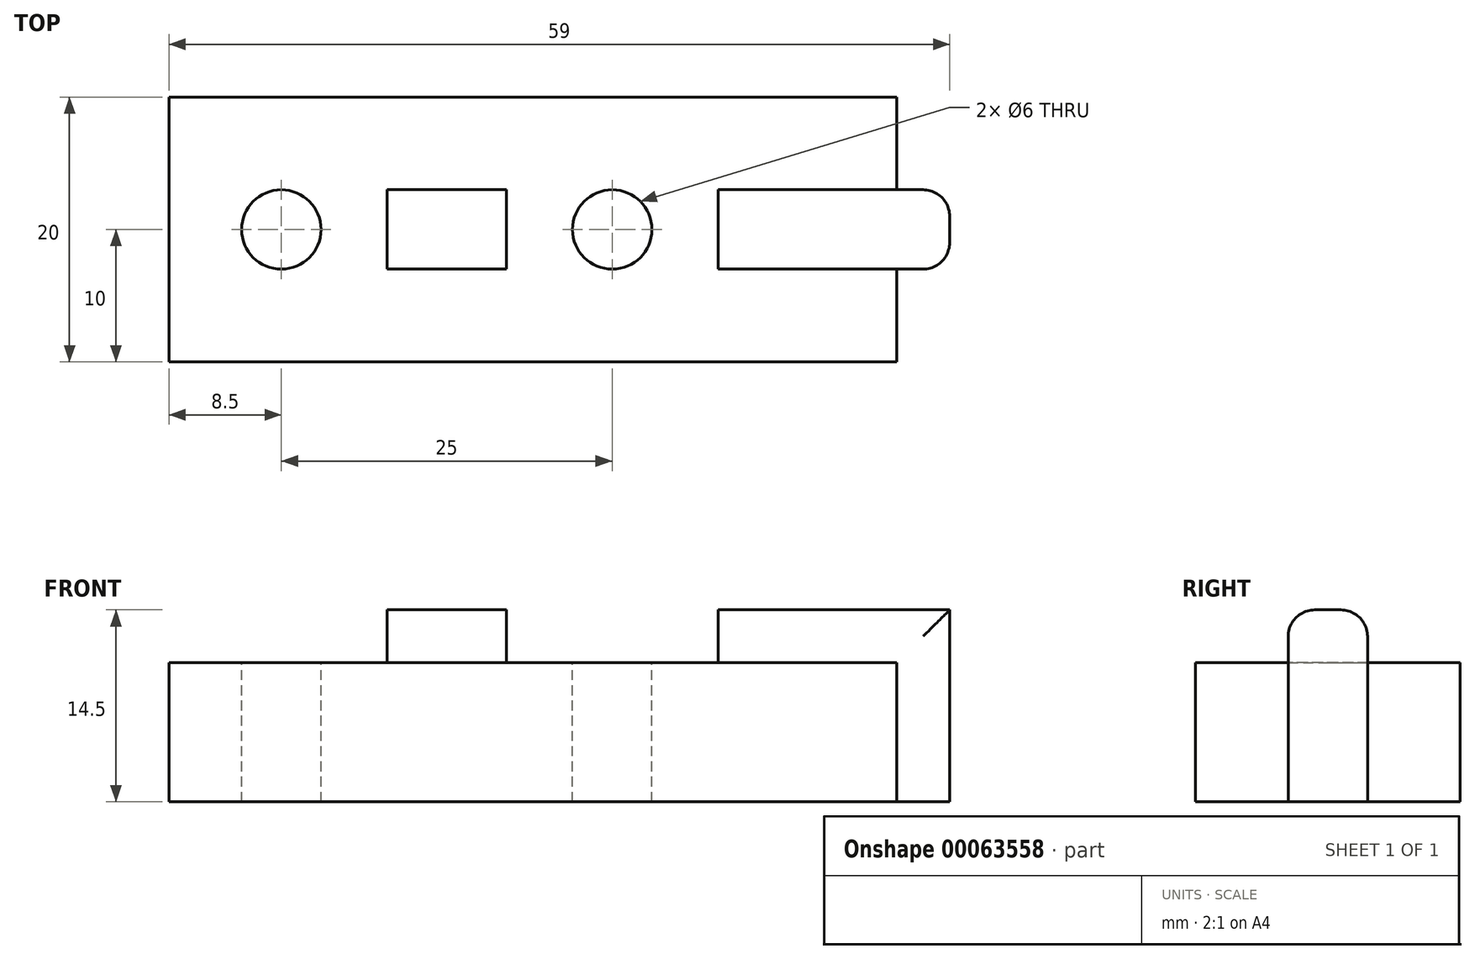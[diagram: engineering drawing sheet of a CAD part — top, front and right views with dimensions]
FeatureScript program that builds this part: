
annotation { "Feature Type Name" : "Feature", "Feature Type Description" : "" }
export const myFeature = defineFeature(function(context is Context, id is Id, definition is map)
    precondition{}
    {
        {
            var Q0;
            Q0=qCreatedBy(makeId("Top.planeOp"),FACE);
            var sketch = newSketch(context, id + "F0", { "sketchPlane" : qUnion([Q0])});
            skLineSegment(sketch, "E0.rect.bottom", {"start": v(-27.5, 10) * mm, "end": v(27.5, 10) * mm});
            skLineSegment(sketch, "E0.rect.top", {"start": v(-27.5, -10) * mm, "end": v(27.5, -10) * mm});
            skLineSegment(sketch, "E0.rect.left", {"start": v(-27.5, 10) * mm, "end": v(-27.5, -10) * mm});
            skLineSegment(sketch, "E0.rect.right", {"start": v(27.5, 10) * mm, "end": v(27.5, -10) * mm});
            skPoint(sketch, "E0.rect.middle", {"position": v(0, 0) * mm});
            skCircle(sketch, "E1", {"center": v(-19, 0) * mm, "radius": 3 * mm});
            skCircle(sketch, "E2", {"center": v(6, 0) * mm, "radius": 3 * mm});
            skPoint(sketch, "E3.visualSharp", {"position": v(31.5, -3) * mm});
            skPoint(sketch, "E4.visualSharp", {"position": v(31.5, 3) * mm});
            skLineSegment(sketch, "E5.bottom", {"start": v(31.5, 3) * mm, "end": v(27.5, 3) * mm});
            skLineSegment(sketch, "E5.top", {"start": v(31.5, -3) * mm, "end": v(27.5, -3) * mm});
            skLineSegment(sketch, "E5.left", {"start": v(31.5, 3) * mm, "end": v(31.5, -3) * mm});
            skLineSegment(sketch, "E5.right", {"start": v(27.5, 3) * mm, "end": v(27.5, -3) * mm});
            skPoint(sketch, "E6", {"position": v(31.5, 0) * mm});
            skPoint(sketch, "E7", {"position": v(27.5, 0) * mm});
            skLineSegment(sketch, "E8", {"start": v(31.5, 0) * mm, "end": v(27.5, 0) * mm, "construction": true});
            skLineSegment(sketch, "E9.bottom", {"start": v(27.5, 3) * mm, "end": v(27.5, 3) * mm});
            skLineSegment(sketch, "E9.top", {"start": v(27.5, -3) * mm, "end": v(27.5, -3) * mm});
            skLineSegment(sketch, "E10.bottom", {"start": v(27.5, 3) * mm, "end": v(14, 3) * mm});
            skLineSegment(sketch, "E10.top", {"start": v(27.5, -3) * mm, "end": v(14, -3) * mm});
            skLineSegment(sketch, "E10.right", {"start": v(14, 3) * mm, "end": v(14, -3) * mm});
            skLineSegment(sketch, "E11.bottom", {"start": v(-2, -3) * mm, "end": v(-11, -3) * mm});
            skLineSegment(sketch, "E11.top", {"start": v(-2, 3) * mm, "end": v(-11, 3) * mm});
            skLineSegment(sketch, "E11.left", {"start": v(-2, -3) * mm, "end": v(-2, 3) * mm});
            skLineSegment(sketch, "E11.right", {"start": v(-11, -3) * mm, "end": v(-11, 3) * mm});
            skLineSegment(sketch, "E12", {"start": v(6, 0) * mm, "end": v(-2, 0) * mm, "construction": true});
            skLineSegment(sketch, "E13", {"start": v(-11, 0) * mm, "end": v(-19, 0) * mm, "construction": true});
            skLineSegment(sketch, "E14", {"start": v(6, 0) * mm, "end": v(14, 0) * mm, "construction": true});
            skSolve(sketch);
        }
        {
            var Q0;
            Q0 = qSketchRegion(id + "F0", true);
            var Q1;
            Q1=makeQuery(id+"F0.imprint","IMPRINT",FACE,{"disambiguationData":[TD([[makeQuery(id+"F0.imprint","IMPRINT",EDGE,{"derivedFrom":sQuery(id+"F0.wireOp",EDGE,"E11.bottom")}),-1.0]])]});
            extrude(context, id + "F1", {"entities" : qUnion([Q0, Q1]), "oppositeDirection" : true, "depth" : 10.5 * mm});
        }
        {
            var Q0;
            Q0=makeQuery(id+"F0.imprint","IMPRINT",FACE,{"disambiguationData":[TD([[makeQuery(id+"F0.imprint","IMPRINT",EDGE,{"derivedFrom":sQuery(id+"F0.wireOp",EDGE,"E10.bottom")}),1.0]])]});
            var Q1;
            Q1=makeQuery(id+"F0.imprint","IMPRINT",FACE,{"disambiguationData":[TD([[makeQuery(id+"F0.imprint","IMPRINT",EDGE,{"derivedFrom":sQuery(id+"F0.wireOp",EDGE,"E5.bottom")}),1.0]])]});
            var Q2;
            Q2=makeQuery(id+"F0.imprint","IMPRINT",FACE,{"disambiguationData":[TD([[makeQuery(id+"F0.imprint","IMPRINT",EDGE,{"derivedFrom":sQuery(id+"F0.wireOp",EDGE,"E11.bottom")}),-1.0]])]});
            extrude(context, id + "F2", {"entities" : qUnion([Q0, Q1, Q2]), "operationType" : NewBodyOperationType.ADD, "depth" : 4 * mm});
        }
        {
            var Q0;
            Q0=makeQuery(id+"F2.opExtrude","CAP_EDGE",EDGE,{"disambiguationData":[OSD([sQuery(id+"F0.wireOp",EDGE,"E5.top"),sQuery(id+"F0.wireOp",EDGE,"E10.top")])],"isStart":false});
            var Q1;
            Q1=makeQuery(id+"F2.opExtrude","CAP_EDGE",EDGE,{"disambiguationData":[OSD([sQuery(id+"F0.wireOp",EDGE,"E5.bottom"),sQuery(id+"F0.wireOp",EDGE,"E10.bottom")])],"isStart":false});
            var Q2;
            {var subQ0=sQuery(id+"F0.wireOp",EDGE,"E5.left");var subQ1=sQuery(id+"F0.wireOp",EDGE,"E5.bottom");Q2=makeQuery(id+"F2.boolean.opBoolean","MERGE",EDGE,{"derivedFrom":[makeQuery(id+"F1.opExtrude","SWEPT_EDGE",EDGE,{"disambiguationData":[OSD([subQ1,subQ0])]}),makeQuery(id+"F2.opExtrude","SWEPT_EDGE",EDGE,{"disambiguationData":[OSD([subQ1,subQ0])]})]});}
            var Q3;
            {var subQ0=sQuery(id+"F0.wireOp",EDGE,"E5.left");var subQ1=sQuery(id+"F0.wireOp",EDGE,"E5.top");Q3=makeQuery(id+"F2.boolean.opBoolean","MERGE",EDGE,{"derivedFrom":[makeQuery(id+"F1.opExtrude","SWEPT_EDGE",EDGE,{"disambiguationData":[OSD([subQ1,subQ0])]}),makeQuery(id+"F2.opExtrude","SWEPT_EDGE",EDGE,{"disambiguationData":[OSD([subQ1,subQ0])]})]});}
            var Q4;
            Q4=makeQuery(id+"F2.opExtrude","CAP_EDGE",EDGE,{"disambiguationData":[OSD([sQuery(id+"F0.wireOp",EDGE,"E11.top")])],"isStart":false});
            var Q5;
            Q5=makeQuery(id+"F2.opExtrude","CAP_EDGE",EDGE,{"disambiguationData":[OSD([sQuery(id+"F0.wireOp",EDGE,"E11.bottom")])],"isStart":false});
            fillet(context, id + "F3", {"entities" : qUnion([Q0, Q1, Q2, Q3, Q4, Q5]), "radius" : 2 * mm, "tangentPropagation" : true, "allowEdgeOverflow" : false});
        }
    });
